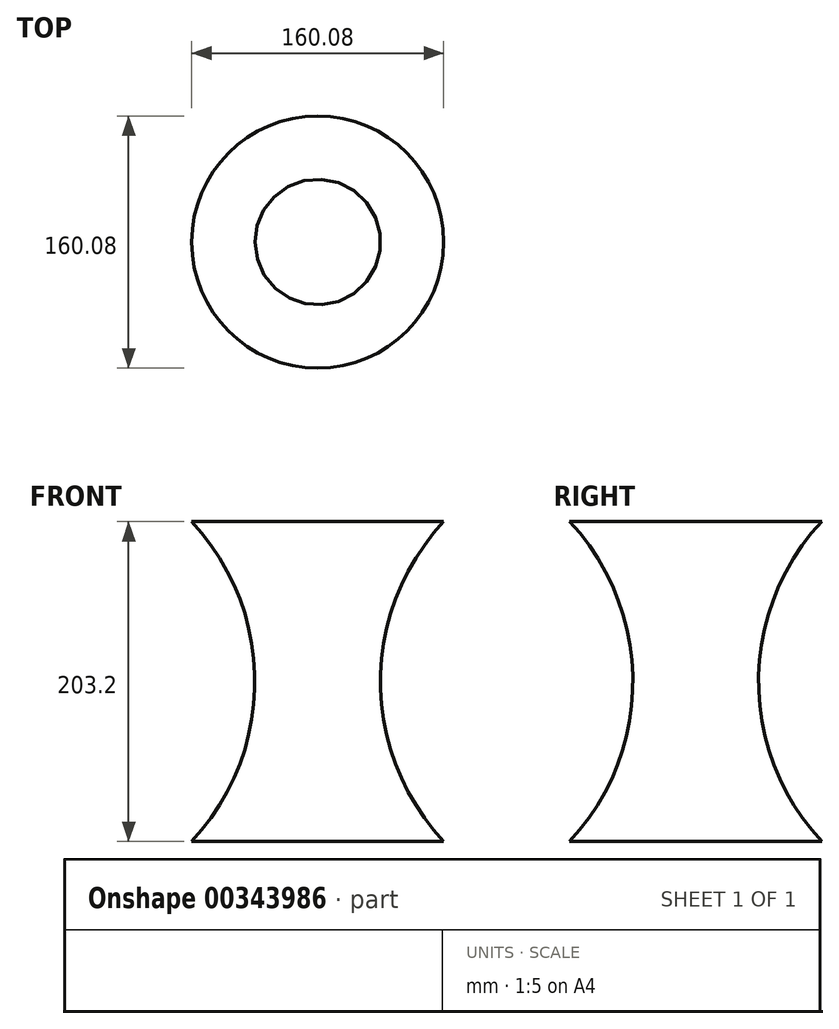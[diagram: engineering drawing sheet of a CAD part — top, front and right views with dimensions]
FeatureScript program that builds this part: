
annotation { "Feature Type Name" : "Feature", "Feature Type Description" : "" }
export const myFeature = defineFeature(function(context is Context, id is Id, definition is map)
    precondition{}
    {
        {
            var Q0;
            Q0=qCreatedBy(makeId("Right.planeOp"),FACE);
            var sketch = newSketch(context, id + "F0", { "sketchPlane" : qUnion([Q0])});
            skLineSegment(sketch, "E0", {"start": v(0, 95.38) * mm, "end": v(0, -97.3) * mm});
            skArc(sketch, "E1", {"start": v(80.04, 101.6) * mm, "mid": v(39.9, 0) * mm, "end": v(80.04, -101.6) * mm});
            skSolve(sketch);
        }
        {
            var Q0;
            Q0=sQuery(id+"F0.wireOp",EDGE,"E1");
            var Q1;
            Q1=sQuery(id+"F0.wireOp",EDGE,"E0");
            revolve(context, id + "F1", {"bodyType" : ToolBodyType.SURFACE, "surfaceEntities" : qUnion([Q0]), "axis" : qUnion([Q1]), "revolveType" : RevolveType.FULL});
        }
    });
